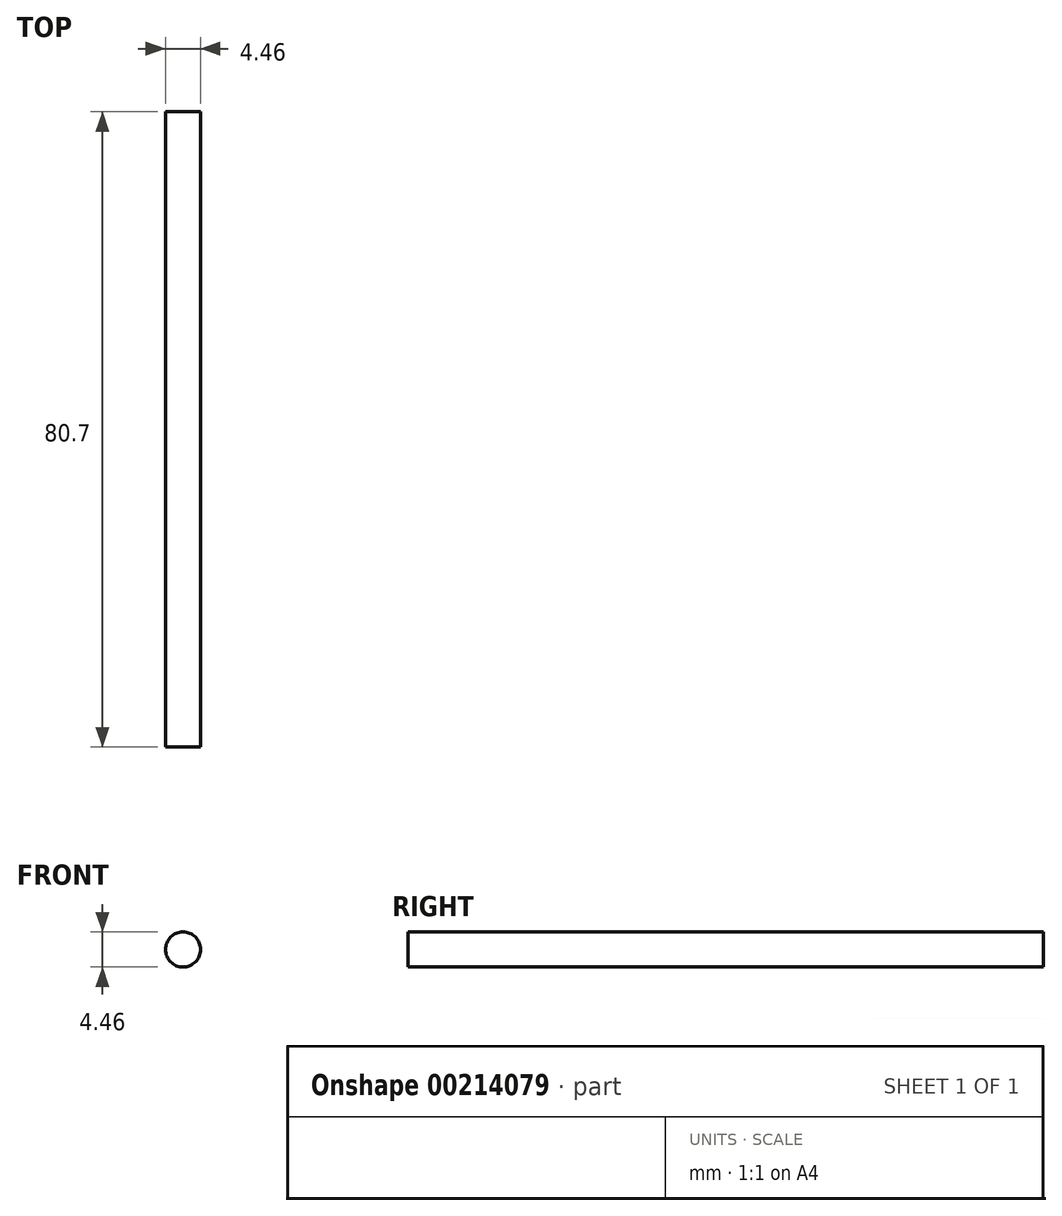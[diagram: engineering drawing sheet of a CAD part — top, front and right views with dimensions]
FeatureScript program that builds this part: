
annotation { "Feature Type Name" : "Feature", "Feature Type Description" : "" }
export const myFeature = defineFeature(function(context is Context, id is Id, definition is map)
    precondition{}
    {
        {
            var Q0;
            Q0=qCreatedBy(makeId("Front.planeOp"),FACE);
            var sketch = newSketch(context, id + "F0", { "sketchPlane" : qUnion([Q0])});
            skCircle(sketch, "E0", {"center": v(0, 0) * mm, "radius": 2.23 * mm});
            skSolve(sketch);
        }
        {
            var Q0;
            Q0=makeQuery(id+"F0.imprint","IMPRINT",FACE,{"disambiguationData":[TD([[makeQuery(id+"F0.imprint","IMPRINT",EDGE,{"derivedFrom":sQuery(id+"F0.wireOp",EDGE,"E0")}),1.0]])]});
            var Q1;
            Q1=sQuery(id+"F0.wireOp",EDGE,"E0");
            extrude(context, id + "F1", {"entities" : qUnion([Q0]), "surfaceEntities" : qUnion([Q1]), "depth" : 80.7 * mm});
        }
    });
